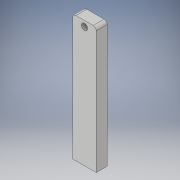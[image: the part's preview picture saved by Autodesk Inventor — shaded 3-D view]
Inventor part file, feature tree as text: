
AUTODESK INVENTOR PART (.ipt)
format: ipt  version: 2019 (Build 230136000, 136)  size: 116,736 bytes
history: native  units: mm
features: extrude x2, sketch x2
ambient origin geometry x8: Origin, YZ Plane, XZ Plane, XY Plane, X Axis, Y Axis, Z Axis, Center Point
bodies: Solid1 (feature_tree)
feature tree (4):
  extrude  "Extrusion1"  Depth=15.0mm
  extrude  "Extrusion2"  Depth=7.0mm
  sketch  "Sketch1"  dims[d0=4.0mm d1=15.0mm]
  sketch  "Sketch2"  dims[d2=7.0mm d3=7.5mm d4=3.5mm d5=2.0mm d6=7.0mm d7=0.0mm d8=0.0mm d9=0.0mm d10=73.5mm d11=0.0mm]
